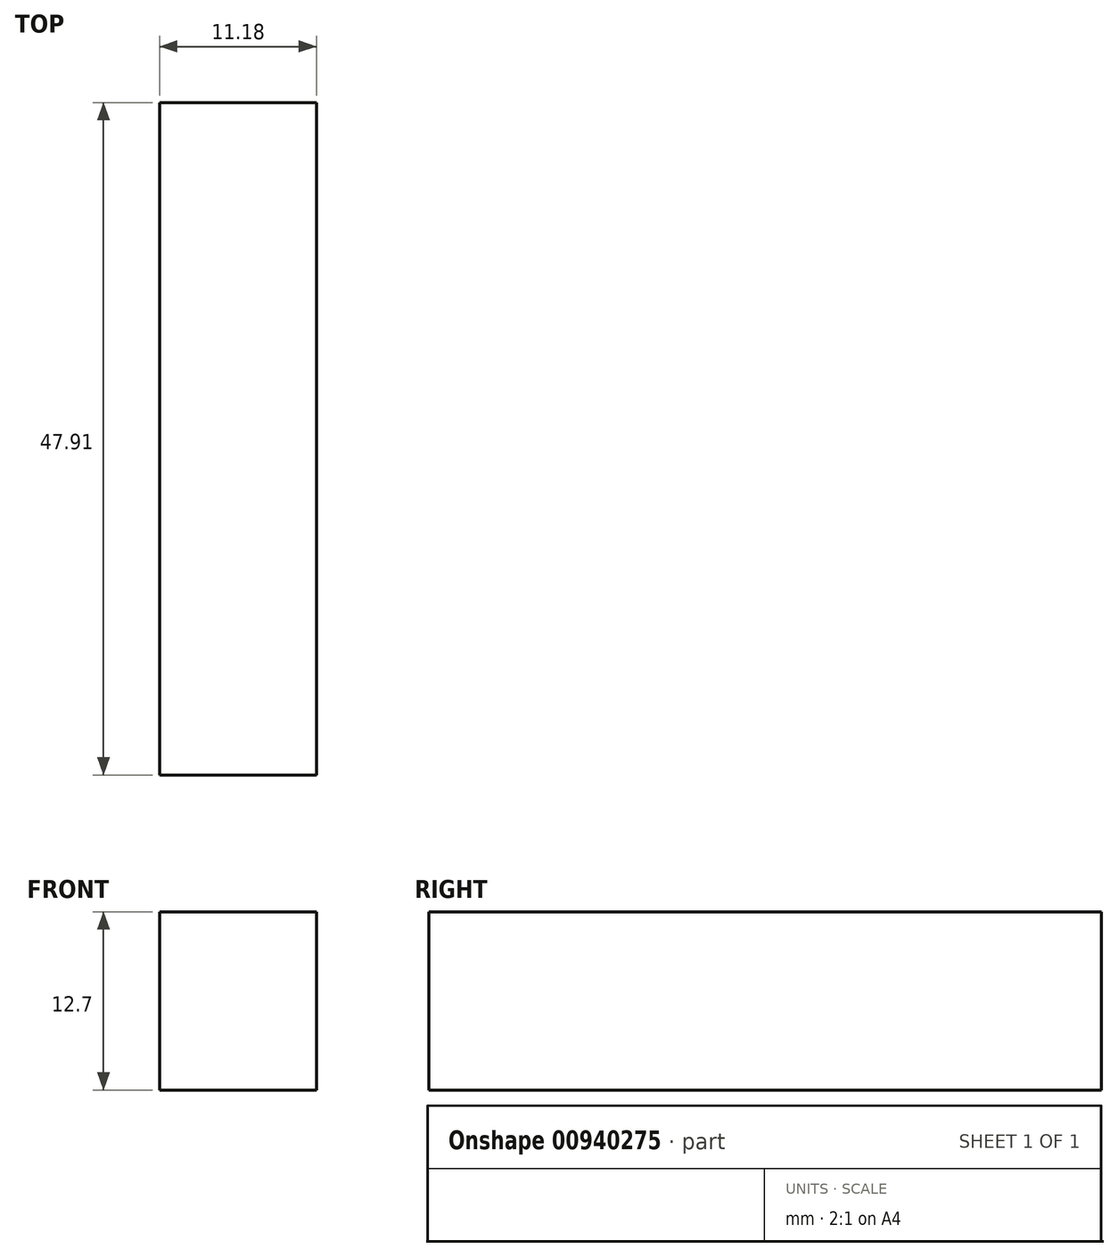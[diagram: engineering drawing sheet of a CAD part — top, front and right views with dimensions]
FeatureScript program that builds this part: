
annotation { "Feature Type Name" : "Feature", "Feature Type Description" : "" }
export const myFeature = defineFeature(function(context is Context, id is Id, definition is map)
    precondition{}
    {
        {
            var Q0;
            Q0=qCreatedBy(makeId("Top.planeOp"),FACE);
            var sketch = newSketch(context, id + "F0", { "sketchPlane" : qUnion([Q0])});
            skLineSegment(sketch, "E0.bottom", {"start": v(-66.77, -27.24) * mm, "end": v(-55.6, -27.24) * mm});
            skLineSegment(sketch, "E0.top", {"start": v(-66.77, 20.67) * mm, "end": v(-55.6, 20.67) * mm});
            skLineSegment(sketch, "E0.left", {"start": v(-66.77, -27.24) * mm, "end": v(-66.77, 20.67) * mm});
            skLineSegment(sketch, "E0.right", {"start": v(-55.6, -27.24) * mm, "end": v(-55.6, 20.67) * mm});
            skSolve(sketch);
        }
        {
            var Q0;
            Q0 = qSketchRegion(id + "F0", true);
            extrude(context, id + "F1", {"entities" : qUnion([Q0]), "depth" : 12.7 * mm, "offsetDistance" : 25.4 * mm});
        }
    });
